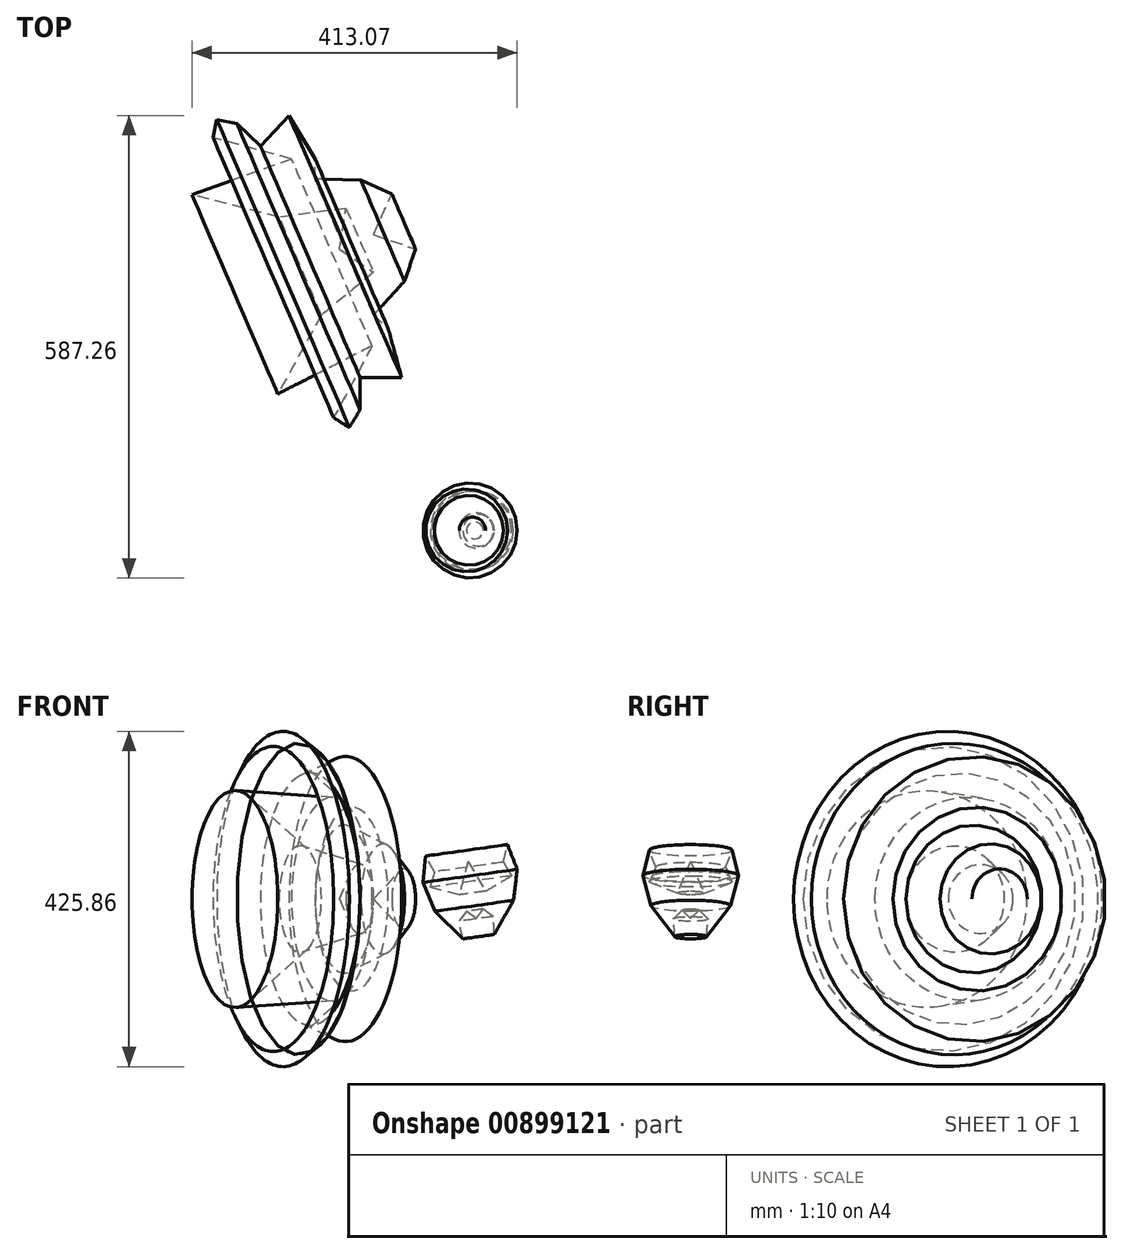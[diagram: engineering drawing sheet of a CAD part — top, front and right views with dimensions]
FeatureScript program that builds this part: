
annotation { "Feature Type Name" : "Feature", "Feature Type Description" : "" }
export const myFeature = defineFeature(function(context is Context, id is Id, definition is map)
    precondition{}
    {
        {
            var Q0;
            Q0=qCreatedBy(makeId("Front.planeOp"),FACE);
            var sketch = newSketch(context, id + "F0", { "sketchPlane" : qUnion([Q0])});
            skLineSegment(sketch, "E0", {"start": v(-10.2, 48.07) * mm, "end": v(-21.3, 5.46) * mm});
            skLineSegment(sketch, "E1", {"start": v(-21.3, 5.46) * mm, "end": v(-58.27, 15.1) * mm});
            skLineSegment(sketch, "E2", {"start": v(-58.27, 15.1) * mm, "end": v(-56.53, 21.78) * mm});
            skLineSegment(sketch, "E3", {"start": v(-56.53, 21.78) * mm, "end": v(-53.01, 34.7) * mm});
            skLineSegment(sketch, "E4", {"start": v(-53.01, 34.7) * mm, "end": v(-64.13, 54.66) * mm});
            skLineSegment(sketch, "E5", {"start": v(-64.13, 54.66) * mm, "end": v(-67.43, 21.1) * mm});
            skLineSegment(sketch, "E6", {"start": v(-67.43, 21.1) * mm, "end": v(-52.2, -15.54) * mm});
            skLineSegment(sketch, "E7", {"start": v(-52.2, -15.54) * mm, "end": v(-16.78, -50.54) * mm});
            skLineSegment(sketch, "E8", {"start": v(-16.78, -50.54) * mm, "end": v(-21.93, -28.3) * mm});
            skLineSegment(sketch, "E9", {"start": v(-21.93, -28.3) * mm, "end": v(-12.25, -15.54) * mm});
            skLineSegment(sketch, "E10", {"start": v(-12.25, -15.54) * mm, "end": v(0, -24.83) * mm});
            skLineSegment(sketch, "E11", {"start": v(-10.2, 48.07) * mm, "end": v(0, -24.83) * mm});
            skSolve(sketch);
        }
        {
            var Q0;
            Q0 = qSketchRegion(id + "F0", true);
            var Q1;
            Q1=sQuery(id+"F0.wireOp",EDGE,"E11");
            revolve(context, id + "F1", {"surfaceOperationType" : NewSurfaceOperationType.NEW, "entities" : qUnion([Q0]), "axis" : qUnion([Q1]), "revolveType" : RevolveType.FULL});
        }
        {
            var Q0;
            Q0=qCreatedBy(makeId("Top.planeOp"),FACE);
            var sketch = newSketch(context, id + "F2", { "sketchPlane" : qUnion([Q0])});
            skLineSegment(sketch, "E12", {"start": v(-251.4, 21.02) * mm, "end": v(-190.14, -71.5) * mm});
            skLineSegment(sketch, "E13", {"start": v(-190.14, -71.5) * mm, "end": v(-187.74, -4.03) * mm});
            skLineSegment(sketch, "E14", {"start": v(-187.74, -4.03) * mm, "end": v(-217.93, 10.4) * mm});
            skLineSegment(sketch, "E15", {"start": v(-217.93, 10.4) * mm, "end": v(-205.26, -19.38) * mm});
            skLineSegment(sketch, "E16", {"start": v(-205.26, -19.38) * mm, "end": v(-232.74, 14.2) * mm});
            skLineSegment(sketch, "E17", {"start": v(-232.74, 14.2) * mm, "end": v(-228.72, 36.5) * mm});
            skLineSegment(sketch, "E18", {"start": v(-228.72, 36.5) * mm, "end": v(-202.27, 26.1) * mm});
            skLineSegment(sketch, "E19", {"start": v(-202.27, 26.1) * mm, "end": v(-168.23, -9.4) * mm});
            skLineSegment(sketch, "E20", {"start": v(-168.23, -9.4) * mm, "end": v(-168.23, -33.5) * mm});
            skLineSegment(sketch, "E21", {"start": v(-168.23, -33.5) * mm, "end": v(-162.19, 9.77) * mm});
            skLineSegment(sketch, "E22", {"start": v(-162.19, 9.77) * mm, "end": v(-209.48, 44.75) * mm});
            skLineSegment(sketch, "E23", {"start": v(-209.48, 44.75) * mm, "end": v(-231.49, 54.87) * mm});
            skLineSegment(sketch, "E24", {"start": v(-231.49, 54.87) * mm, "end": v(-248.55, 44.07) * mm});
            skLineSegment(sketch, "E25", {"start": v(-248.55, 44.07) * mm, "end": v(-242.3, 22.95) * mm});
            skLineSegment(sketch, "E26", {"start": v(-242.3, 22.95) * mm, "end": v(-259.62, 47.18) * mm});
            skLineSegment(sketch, "E27", {"start": v(-259.62, 47.18) * mm, "end": v(-244.76, 70.03) * mm});
            skLineSegment(sketch, "E28", {"start": v(-244.76, 70.03) * mm, "end": v(-219.59, 70.03) * mm});
            skLineSegment(sketch, "E29", {"start": v(-219.59, 70.03) * mm, "end": v(-188.71, 42.95) * mm});
            skLineSegment(sketch, "E30", {"start": v(-188.71, 42.95) * mm, "end": v(-150.49, 14.63) * mm});
            skLineSegment(sketch, "E31", {"start": v(-150.49, 14.63) * mm, "end": v(-143.16, -42.95) * mm});
            skLineSegment(sketch, "E32", {"start": v(-143.16, -42.95) * mm, "end": v(-167.83, -53.45) * mm});
            skLineSegment(sketch, "E33", {"start": v(-167.83, -53.45) * mm, "end": v(-174.5, -37.77) * mm});
            skLineSegment(sketch, "E34", {"start": v(-174.5, -37.77) * mm, "end": v(-174.5, -64.03) * mm});
            skLineSegment(sketch, "E35", {"start": v(-174.5, -64.03) * mm, "end": v(-185.06, -107.08) * mm});
            skLineSegment(sketch, "E36", {"start": v(-185.06, -107.08) * mm, "end": v(-216.42, -61) * mm});
            skLineSegment(sketch, "E37", {"start": v(-132.02, 234.22) * mm, "end": v(-251.82, 173.43) * mm});
            skLineSegment(sketch, "E38", {"start": v(-251.82, 173.43) * mm, "end": v(-196.52, 273.56) * mm});
            skLineSegment(sketch, "E39", {"start": v(-196.52, 273.56) * mm, "end": v(-130.21, 327.8) * mm});
            skLineSegment(sketch, "E40", {"start": v(-130.21, 327.8) * mm, "end": v(-173.41, 357.26) * mm});
            skLineSegment(sketch, "E41", {"start": v(-173.41, 357.26) * mm, "end": v(-130.21, 375.86) * mm});
            skLineSegment(sketch, "E42", {"start": v(-130.21, 375.86) * mm, "end": v(-76.77, 357.26) * mm});
            skLineSegment(sketch, "E43", {"start": v(-76.77, 357.26) * mm, "end": v(-90.93, 316.57) * mm});
            skLineSegment(sketch, "E44", {"start": v(-90.93, 316.57) * mm, "end": v(-130.21, 273.56) * mm});
            skLineSegment(sketch, "E45", {"start": v(-130.21, 273.56) * mm, "end": v(-111.7, 256.66) * mm});
            skLineSegment(sketch, "E46", {"start": v(-111.7, 256.66) * mm, "end": v(-94.41, 194.04) * mm});
            skLineSegment(sketch, "E47", {"start": v(-94.41, 194.04) * mm, "end": v(-147.25, 194.04) * mm});
            skLineSegment(sketch, "E48", {"start": v(-147.25, 194.04) * mm, "end": v(-147.25, 153.12) * mm});
            skLineSegment(sketch, "E49", {"start": v(-147.25, 153.12) * mm, "end": v(-160.98, 130.8) * mm});
            skLineSegment(sketch, "E50", {"start": v(-160.98, 130.8) * mm, "end": v(-180.9, 143.05) * mm});
            skLineSegment(sketch, "E51", {"start": v(-180.9, 143.05) * mm, "end": v(-132.02, 234.22) * mm});
            skSolve(sketch);
        }
        {
            var Q0;
            Q0 = qSketchRegion(id + "F2", true);
            var Q1;
            Q1=sQuery(id+"F2.wireOp",EDGE,"E41");
            revolve(context, id + "F3", {"surfaceOperationType" : NewSurfaceOperationType.NEW, "entities" : qUnion([Q0]), "axis" : qUnion([Q1]), "revolveType" : RevolveType.FULL});
        }
    });
